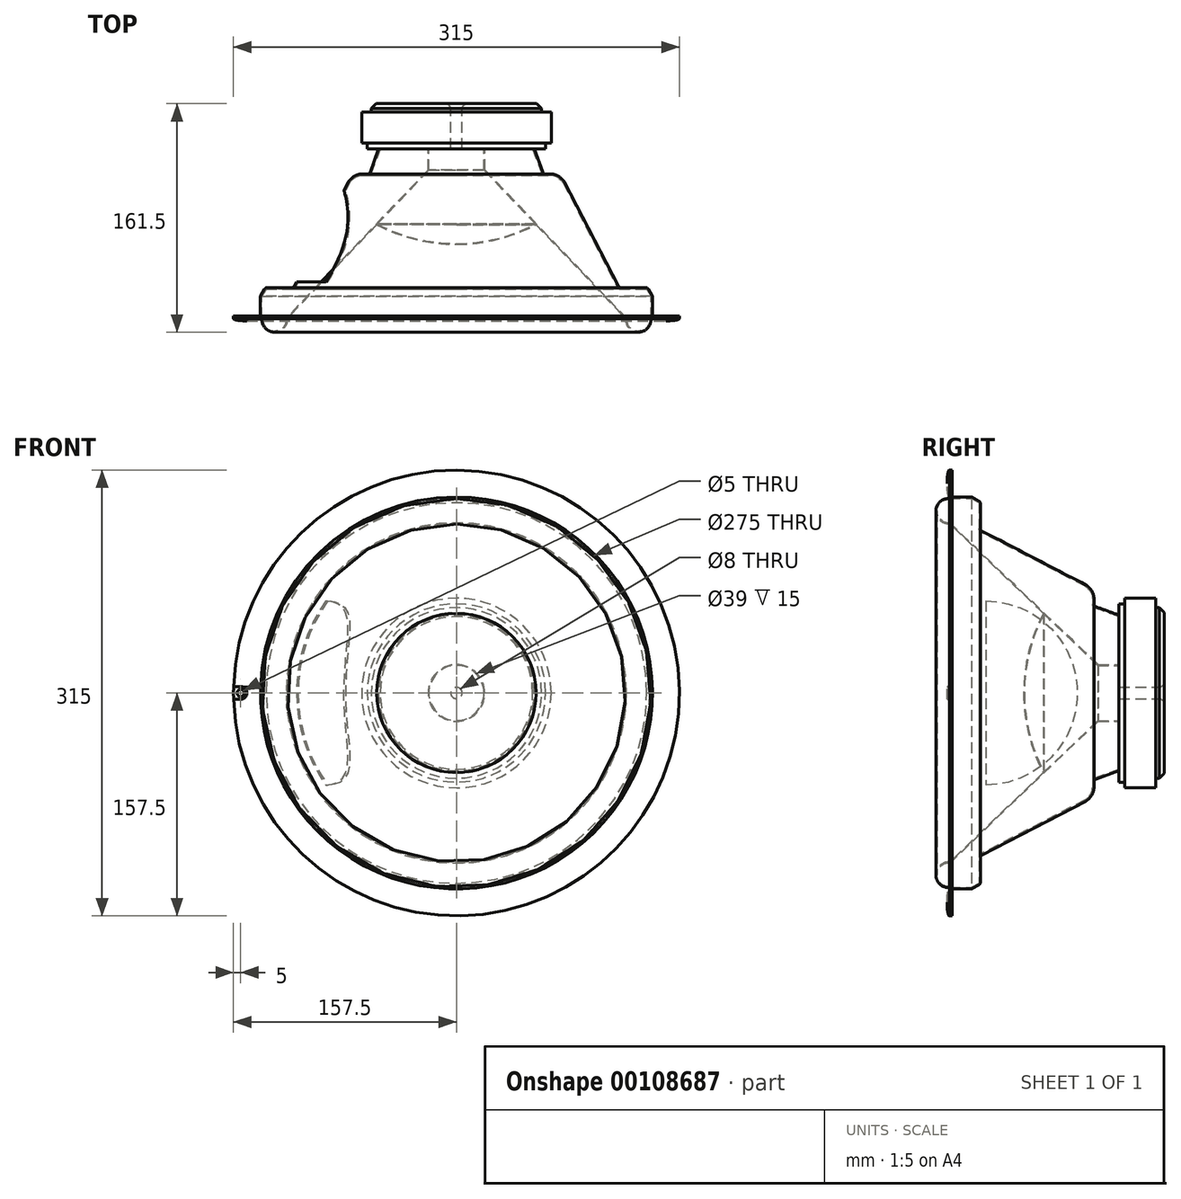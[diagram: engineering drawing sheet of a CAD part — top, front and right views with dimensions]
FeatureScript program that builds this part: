
annotation { "Feature Type Name" : "Feature", "Feature Type Description" : "" }
export const myFeature = defineFeature(function(context is Context, id is Id, definition is map)
    precondition{}
    {
        {
            var Q0;
            Q0=qCreatedBy(makeId("Front.planeOp"),FACE);
            var sketch = newSketch(context, id + "F0", { "sketchPlane" : qUnion([Q0])});
            skCircle(sketch, "E0", {"center": v(0, 0) * mm, "radius": 157.5 * mm});
            skCircle(sketch, "E1", {"center": v(0, 0) * mm, "radius": 152.5 * mm, "construction": true});
            skCircle(sketch, "E2", {"center": v(0, 0) * mm, "radius": 138.5 * mm});
            skCircle(sketch, "E3", {"center": v(0, 0) * mm, "radius": 67 * mm, "construction": true});
            skSolve(sketch);
        }
        {
            var Q0;
            Q0=qCreatedBy(makeId("Front.planeOp"),FACE);
            var sketch = newSketch(context, id + "F1", { "sketchPlane" : qUnion([Q0])});
            skCircle(sketch, "E4", {"center": v(-152.5, 0) * mm, "radius": 2.5 * mm});
            skLineSegment(sketch, "E5", {"start": v(-152.5, 0) * mm, "end": v(0, 0) * mm, "construction": true});
            skLineSegment(sketch, "E6", {"start": v(-157.5, -4.5) * mm, "end": v(-157.5, 4.5) * mm});
            skLineSegment(sketch, "E7", {"start": v(-157.5, 4.5) * mm, "end": v(-152.5, 4.5) * mm});
            skLineSegment(sketch, "E8", {"start": v(-157.5, -4.5) * mm, "end": v(-152.5, -4.5) * mm});
            skArc(sketch, "E9", {"start": v(-152.5, -4.5) * mm, "mid": v(-148, 0) * mm, "end": v(-152.5, 4.5) * mm});
            skCircle(sketch, "E10.0", {"center": v(0, 0) * mm, "radius": 152.5 * mm, "construction": true});
            skCircle(sketch, "E11.0", {"center": v(0, 0) * mm, "radius": 157.5 * mm, "construction": true});
            skSolve(sketch);
        }
        {
            var Q0;
            Q0=qCreatedBy(makeId("Top.planeOp"),FACE);
            var sketch = newSketch(context, id + "F2", { "sketchPlane" : qUnion([Q0])});
            skFitSpline(sketch, "E12", {"points": [v(-157.5, -2) * mm, v(-138.5, -2) * mm], "startDerivative": vector(0, -6) * mm, "endDerivative": vector(0, 6) * mm});
            skLineSegment(sketch, "E13", {"start": v(-148, 0) * mm, "end": v(-148, -14.54) * mm, "construction": true});
            skLineSegment(sketch, "E14", {"start": v(-60.25, 144) * mm, "end": v(-67, 144) * mm});
            skLineSegment(sketch, "E15", {"start": v(138.5, 0) * mm, "end": v(157.5, 0) * mm});
            skLineSegment(sketch, "E16", {"start": v(-157.5, 0) * mm, "end": v(-138.5, 0) * mm});
            skLineSegment(sketch, "E17", {"start": v(-138.5, -2) * mm, "end": v(-138.5, 0) * mm});
            skLineSegment(sketch, "E18", {"start": v(-157.5, -2) * mm, "end": v(-157.5, 0) * mm});
            skLineSegment(sketch, "E19", {"start": v(-138.5, -2) * mm, "end": v(-157.5, -2) * mm, "construction": true});
            skPoint(sketch, "E20", {"position": v(-148, -2) * mm});
            skPoint(sketch, "E21", {"position": v(-148, -3.5) * mm});
            skLineSegment(sketch, "E22", {"start": v(-67, 144) * mm, "end": v(-67, 122) * mm});
            skLineSegment(sketch, "E23", {"start": v(-67, 122) * mm, "end": v(-63, 122) * mm});
            skLineSegment(sketch, "E24", {"start": v(-63, 122) * mm, "end": v(-63, 118) * mm});
            skLineSegment(sketch, "E25", {"start": v(0, 158.38) * mm, "end": v(0, 103.9) * mm, "construction": true});
            skLineSegment(sketch, "E26", {"start": v(-60.25, 144) * mm, "end": v(-60.25, 146.5) * mm});
            skLineSegment(sketch, "E27", {"start": v(-60.25, 146.5) * mm, "end": v(-56.75, 150) * mm});
            skLineSegment(sketch, "E28", {"start": v(-56.75, 150) * mm, "end": v(-8, 150) * mm});
            skLineSegment(sketch, "E29", {"start": v(-63, 118) * mm, "end": v(-55, 118) * mm});
            skLineSegment(sketch, "E30", {"start": v(-55, 118) * mm, "end": v(-60.97, 101.6) * mm});
            skLineSegment(sketch, "E31", {"start": v(-62.85, 100.28) * mm, "end": v(-66.8, 100.28) * mm});
            skLineSegment(sketch, "E32", {"start": v(-73.24, 97.94) * mm, "end": v(-74.5, 96.89) * mm});
            skLineSegment(sketch, "E33", {"start": v(-76.35, 94.57) * mm, "end": v(-114.46, 21.08) * mm});
            skLineSegment(sketch, "E34", {"start": v(-116.24, 20) * mm, "end": v(-133.87, 20) * mm});
            skLineSegment(sketch, "E35", {"start": v(-138.5, 0) * mm, "end": v(-138.5, 13.46) * mm});
            skLineSegment(sketch, "E36", {"start": v(-138.23, 14.47) * mm, "end": v(-135.6, 19) * mm});
            skPoint(sketch, "E37.visualSharp", {"position": v(-70.45, 100.28) * mm});
            skArc(sketch, "E37.filletArc", {"start": v(-66.8, 100.28) * mm, "mid": v(-70.23, 99.68) * mm, "end": v(-73.24, 97.94) * mm});
            skPoint(sketch, "E38.visualSharp", {"position": v(-61.45, 100.28) * mm});
            skArc(sketch, "E38.filletArc", {"start": v(-62.85, 100.28) * mm, "mid": v(-61.7, 100.64) * mm, "end": v(-60.97, 101.6) * mm});
            skPoint(sketch, "E39.visualSharp", {"position": v(-75.65, 95.91) * mm});
            skArc(sketch, "E39.filletArc", {"start": v(-74.5, 96.89) * mm, "mid": v(-75.54, 95.82) * mm, "end": v(-76.35, 94.57) * mm});
            skPoint(sketch, "E40.visualSharp", {"position": v(-115.02, 20) * mm});
            skArc(sketch, "E40.filletArc", {"start": v(-116.24, 20) * mm, "mid": v(-115.2, 20.3) * mm, "end": v(-114.46, 21.08) * mm});
            skPoint(sketch, "E41.visualSharp", {"position": v(-135.02, 20) * mm});
            skArc(sketch, "E41.filletArc", {"start": v(-133.87, 20) * mm, "mid": v(-134.87, 19.73) * mm, "end": v(-135.6, 19) * mm});
            skPoint(sketch, "E42.visualSharp", {"position": v(-138.5, 14) * mm});
            skArc(sketch, "E42.filletArc", {"start": v(-138.23, 14.47) * mm, "mid": v(-138.43, 13.98) * mm, "end": v(-138.5, 13.46) * mm});
            skLineSegment(sketch, "E43.0", {"start": v(-137.5, -1.7) * mm, "end": v(-137.5, 0) * mm});
            skLineSegment(sketch, "E43.1", {"start": v(-137.5, 0) * mm, "end": v(-137.5, 13.73) * mm});
            skArc(sketch, "E43.2", {"start": v(-66.8, 99.28) * mm, "mid": v(-69.89, 98.74) * mm, "end": v(-72.6, 97.18) * mm});
            skLineSegment(sketch, "E43.3", {"start": v(-62.85, 99.28) * mm, "end": v(-66.8, 99.28) * mm});
            skArc(sketch, "E43.4", {"start": v(-62.85, 99.28) * mm, "mid": v(-61.13, 99.82) * mm, "end": v(-60.03, 101.26) * mm});
            skLineSegment(sketch, "E43.5", {"start": v(-53.9, 118.08) * mm, "end": v(-60.03, 101.26) * mm});
            skLineSegment(sketch, "E43.6", {"start": v(-72.6, 97.18) * mm, "end": v(-73.85, 96.12) * mm});
            skArc(sketch, "E43.7", {"start": v(-73.85, 96.12) * mm, "mid": v(-74.76, 95.2) * mm, "end": v(-75.46, 94.1) * mm});
            skLineSegment(sketch, "E43.8", {"start": v(-75.46, 94.1) * mm, "end": v(-113.58, 20.62) * mm});
            skArc(sketch, "E43.9", {"start": v(-116.24, 19) * mm, "mid": v(-114.68, 19.44) * mm, "end": v(-113.58, 20.62) * mm});
            skLineSegment(sketch, "E43.10", {"start": v(-116.24, 19) * mm, "end": v(-134.45, 19) * mm});
            skLineSegment(sketch, "E43.11", {"start": v(-137.5, 13.73) * mm, "end": v(-134.45, 19) * mm});
            skLineSegment(sketch, "E44", {"start": v(-138.5, -2) * mm, "end": v(-137.8, -2) * mm});
            skPoint(sketch, "E45.visualSharp", {"position": v(-137.5, -2) * mm});
            skArc(sketch, "E45.filletArc", {"start": v(-137.8, -2) * mm, "mid": v(-137.59, -1.91) * mm, "end": v(-137.5, -1.7) * mm});
            skLineSegment(sketch, "E46", {"start": v(-4, 118.08) * mm, "end": v(-4, 146) * mm});
            skLineSegment(sketch, "E47", {"start": v(-4, 150) * mm, "end": v(0, 150) * mm, "construction": true});
            skLineSegment(sketch, "E48", {"start": v(-53.9, 118.08) * mm, "end": v(-4, 118.08) * mm});
            skPoint(sketch, "E49.visualSharp", {"position": v(-4, 150) * mm});
            skArc(sketch, "E49.filletArc", {"start": v(-4, 146) * mm, "mid": v(-5.17, 148.83) * mm, "end": v(-8, 150) * mm});
            skSolve(sketch);
        }
        {
            var Q0;
            Q0=makeQuery(id+"F2.imprint","IMPRINT",FACE,{"disambiguationData":[TD([[makeQuery(id+"F2.imprint","IMPRINT",EDGE,{"derivedFrom":sQuery(id+"F2.wireOp",EDGE,"E12")}),1.0]])]});
            var Q1;
            Q1=makeQuery(id+"F2.imprint","IMPRINT",FACE,{"disambiguationData":[TD([[makeQuery(id+"F2.imprint","IMPRINT",EDGE,{"derivedFrom":sQuery(id+"F2.wireOp",EDGE,"E17")}),-1.0]])]});
            var Q2;
            Q2=makeQuery(id+"F2.imprint","IMPRINT",FACE,{"disambiguationData":[TD([[makeQuery(id+"F2.imprint","IMPRINT",EDGE,{"derivedFrom":sQuery(id+"F2.wireOp",EDGE,"E14")}),1.0]])]});
            var Q3;
            Q3=sQuery(id+"F0.wireOp",EDGE,"E2");
            revolve(context, id + "F3", {"entities" : qUnion([Q0, Q1, Q2]), "axis" : qUnion([Q3]), "revolveType" : RevolveType.FULL});
        }
        {
            var Q0;
            Q0=makeQuery(id+"F1.imprint","IMPRINT",FACE,{"disambiguationData":[TD([[makeQuery(id+"F1.imprint","IMPRINT",EDGE,{"derivedFrom":sQuery(id+"F1.wireOp",EDGE,"E4")}),1.0]])]});
            extrude(context, id + "F4", {"entities" : qUnion([Q0]), "operationType" : NewBodyOperationType.REMOVE, "endBound" : BoundingType.THROUGH_ALL, "depth" : 25 * mm});
        }
        {
            var Q0;
            Q0=makeQuery(id+"F1.imprint","IMPRINT",FACE,{"disambiguationData":[TD([[makeQuery(id+"F1.imprint","IMPRINT",EDGE,{"derivedFrom":sQuery(id+"F1.wireOp",EDGE,"E4")}),-1.0]])]});
            var Q1;
            Q1=makeQuery(id+"F3.opRevolve","SWEPT_FACE",FACE,{"disambiguationData":[OSD([sQuery(id+"F2.wireOp",EDGE,"E12")])]});
            var Q2;
            Q2=makeQuery(id+"F3.opRevolve","SWEPT_BODY",BODY,{"disambiguationData":[OSD([sQuery(id+"F2.wireOp",EDGE,"E12"),sQuery(id+"F2.wireOp",EDGE,"E16"),sQuery(id+"F2.wireOp",EDGE,"E17"),sQuery(id+"F2.wireOp",EDGE,"E18")])]});
            var Q3;
            Q3=qCreatedBy(makeId("Top.planeOp"),FACE);
            var Q4;
            Q4=makeQuery(id+"F3.opRevolve","SWEPT_BODY",BODY,{"disambiguationData":[OSD([sQuery(id+"F2.wireOp",EDGE,"HXbbiPvt-2vBx-SDOX-ASnO-lKyWj4IHX7Yn"),sQuery(id+"F2.wireOp",EDGE,"E12")])]});
            extrude(context, id + "F5", {"entities" : qUnion([Q0]), "operationType" : NewBodyOperationType.REMOVE, "endBound" : BoundingType.UP_TO_NEXT, "endBoundEntityFace" : qUnion([Q1]), "endBoundEntityBody" : qUnion([Q2]), "depth" : 3.88 * mm, "hasSecondDirection" : true, "secondDirectionOppositeDirection" : false, "secondDirectionBoundEntityFace" : qUnion([Q3]), "secondDirectionBoundEntityBody" : qUnion([Q4]), "secondDirectionDepth" : 2 * mm});
        }
        {
            var Q0;
            Q0=qCreatedBy(makeId("Right.planeOp"),FACE);
            var sketch = newSketch(context, id + "F6", { "sketchPlane" : qUnion([Q0])});
            skLineSegment(sketch, "E50", {"start": v(24, 112.95) * mm, "end": v(88.57, 79.46) * mm, "construction": true});
            skLineSegment(sketch, "E51", {"start": v(88.57, -79.46) * mm, "end": v(24, -112.95) * mm, "construction": true});
            skLineSegment(sketch, "E52", {"start": v(88.57, 79.46) * mm, "end": v(88.57, -79.46) * mm, "construction": true});
            skLineSegment(sketch, "E53", {"start": v(24, 112.95) * mm, "end": v(24, -112.95) * mm, "construction": true});
            skArc(sketch, "E54", {"start": v(24, -65.1) * mm, "mid": v(88.57, 0) * mm, "end": v(24, 65.1) * mm});
            skLineSegment(sketch, "E55", {"start": v(24, 65.1) * mm, "end": v(24, -65.1) * mm});
            skSolve(sketch);
        }
        {
            var Q0;
            Q0=makeQuery(id+"F6.imprint","IMPRINT",FACE,{"disambiguationData":[TD([[makeQuery(id+"F6.imprint","IMPRINT",EDGE,{"derivedFrom":sQuery(id+"F6.wireOp",EDGE,"E54")}),1.0]])]});
            var Q1;
            Q1=makeQuery(id+"F3.opRevolve","SWEPT_FACE",FACE,{"disambiguationData":[OSD([sQuery(id+"F2.wireOp",EDGE,"E33")])]});
            extrude(context, id + "F7", {"entities" : qUnion([Q0]), "operationType" : NewBodyOperationType.REMOVE, "endBound" : BoundingType.UP_TO_SURFACE, "oppositeDirection" : true, "endBoundEntityFace" : qUnion([Q1]), "depth" : 300 * mm});
        }
        {
            var Q0;
            Q0=qCreatedBy(makeId("Right.planeOp"),FACE);
            var sketch = newSketch(context, id + "F8", { "sketchPlane" : qUnion([Q0])});
            skLineSegment(sketch, "E56.0", {"start": v(0, 157.5) * mm, "end": v(0, -157.5) * mm, "construction": true});
            skLineSegment(sketch, "E57", {"start": v(-11.5, 157.96) * mm, "end": v(-11.5, -148.62) * mm, "construction": true});
            skLineSegment(sketch, "E58.0", {"start": v(-1.7, 137.5) * mm, "end": v(-1.7, -137.5) * mm, "construction": true});
            skLineSegment(sketch, "E59", {"start": v(-89.8, -119.5) * mm, "end": v(37.13, -119.5) * mm, "construction": true});
            skArc(sketch, "E60", {"start": v(-1.7, -119.5) * mm, "mid": v(-11.5, -128.5) * mm, "end": v(-1.7, -137.5) * mm});
            skArc(sketch, "E61.0", {"start": v(-1.76, -120.2) * mm, "mid": v(-10.8, -128.5) * mm, "end": v(-1.76, -136.8) * mm});
            skLineSegment(sketch, "E62", {"start": v(-1.7, -137.5) * mm, "end": v(-1.76, -136.8) * mm});
            skLineSegment(sketch, "E63", {"start": v(-1.76, -120.2) * mm, "end": v(-1.7, -119.5) * mm});
            skSolve(sketch);
        }
        {
            var Q0;
            Q0=makeQuery(id+"F8.imprint","IMPRINT",FACE,{"disambiguationData":[TD([[makeQuery(id+"F8.imprint","IMPRINT",EDGE,{"derivedFrom":sQuery(id+"F8.wireOp",EDGE,"E60")}),1.0]])]});
            var Q1;
            Q1=sQuery(id+"F0.wireOp",EDGE,"E2");
            revolve(context, id + "F9", {"entities" : qUnion([Q0]), "axis" : qUnion([Q1]), "revolveType" : RevolveType.FULL});
        }
        {
            var Q0;
            Q0=qCreatedBy(makeId("Right.planeOp"),FACE);
            var sketch = newSketch(context, id + "F10", { "sketchPlane" : qUnion([Q0])});
            skLineSegment(sketch, "E64.0", {"start": v(-1.7, 119.5) * mm, "end": v(-1.7, -119.5) * mm});
            skLineSegment(sketch, "E65.0", {"start": v(-1.7, 119.5) * mm, "end": v(-1.7, -119.5) * mm, "construction": true});
            skLineSegment(sketch, "E66.0", {"start": v(24, 112.95) * mm, "end": v(88.57, 79.46) * mm, "construction": true});
            skLineSegment(sketch, "E66.1", {"start": v(88.57, -79.46) * mm, "end": v(24, -112.95) * mm, "construction": true});
            skLineSegment(sketch, "E67.0", {"start": v(118, 55) * mm, "end": v(118, -55) * mm});
            skLineSegment(sketch, "E68.0", {"start": v(118, 55) * mm, "end": v(118, -55) * mm, "construction": true});
            skLineSegment(sketch, "E69", {"start": v(118, 0) * mm, "end": v(-91.92, 0) * mm, "construction": true});
            skPoint(sketch, "E69.endSnap0", {"position": v(118, 0) * mm});
            skLineSegment(sketch, "E70", {"start": v(118, -19.5) * mm, "end": v(103, -19.5) * mm});
            skLineSegment(sketch, "E71", {"start": v(103, -19.5) * mm, "end": v(-1.7, -119.5) * mm});
            skLineSegment(sketch, "E72.0", {"start": v(103.2, -20) * mm, "end": v(-1.35, -119.86) * mm});
            skLineSegment(sketch, "E72.1", {"start": v(118, -20) * mm, "end": v(103.2, -20) * mm});
            skLineSegment(sketch, "E73", {"start": v(118, -20) * mm, "end": v(118, -19.5) * mm});
            skLineSegment(sketch, "E74", {"start": v(-1.35, -119.86) * mm, "end": v(-1.7, -119.5) * mm});
            skArc(sketch, "E75", {"start": v(50.59, 0) * mm, "mid": v(54.12, -28.98) * mm, "end": v(64.5, -56.28) * mm});
            skLineSegment(sketch, "E76", {"start": v(50.59, -43.75) * mm, "end": v(50.59, 35.54) * mm, "construction": true});
            skArc(sketch, "E77.0", {"start": v(51.09, 0) * mm, "mid": v(54.6, -28.86) * mm, "end": v(64.94, -56.04) * mm});
            skLineSegment(sketch, "E78", {"start": v(64.5, -56.28) * mm, "end": v(64.94, -56.04) * mm});
            skLineSegment(sketch, "E79", {"start": v(50.59, 0) * mm, "end": v(51.09, 0) * mm});
            skSolve(sketch);
        }
        {
            var Q0;
            {var subQ0=sQuery(id+"F10.wireOp",EDGE,"E75");Q0=makeQuery(id+"F10.imprint","IMPRINT",FACE,{"disambiguationData":[TD([[makeQuery(id+"F10.imprint","IMPRINT",EDGE,{"derivedFrom":subQ0}),1.0]])]});}
            var Q1;
            {var subQ3=sQuery(id+"F10.wireOp",EDGE,"E70");Q1=makeQuery(id+"F10.imprint","IMPRINT",FACE,{"disambiguationData":[TD([[makeQuery(id+"F10.imprint","IMPRINT",EDGE,{"derivedFrom":subQ3}),1.0]])]});}
            var Q2;
            Q2=sQuery(id+"F10.wireOp",EDGE,"E69");
            revolve(context, id + "F11", {"entities" : qUnion([Q0, Q1]), "axis" : qUnion([Q2]), "revolveType" : RevolveType.FULL});
        }
    });
